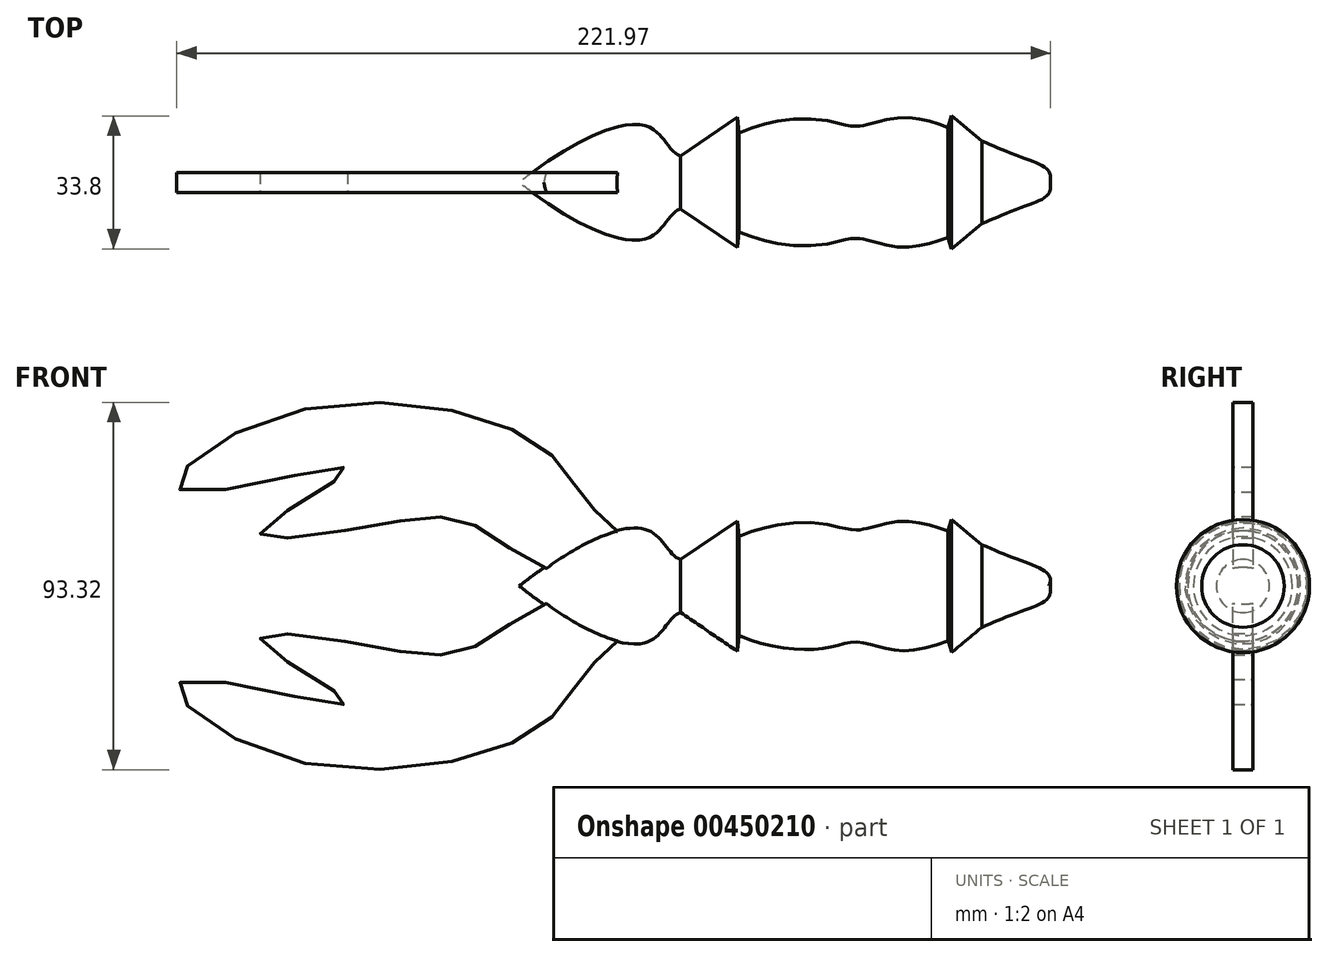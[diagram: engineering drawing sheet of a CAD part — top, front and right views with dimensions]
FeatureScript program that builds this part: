
annotation { "Feature Type Name" : "Feature", "Feature Type Description" : "" }
export const myFeature = defineFeature(function(context is Context, id is Id, definition is map)
    precondition{}
    {
        {
            var Q0;
            Q0=qCreatedBy(makeId("Front.planeOp"),FACE);
            var sketch = newSketch(context, id + "F0", { "sketchPlane" : qUnion([Q0])});
            skFitSpline(sketch, "E0", {"points": [v(-77.57, 0) * mm, v(-44.09, 13.8) * mm, v(-36.58, 6.72) * mm, v(-20.7, 13) * mm, v(0, 15.78) * mm, v(8.64, 14.26) * mm, v(21, 16.45) * mm, v(48.3, 7.05) * mm, v(57.04, 0) * mm], "startDerivative": vector(233.97, 184.67) * mm, "endDerivative": vector(-52.98, -112.96) * mm});
            skLineSegment(sketch, "E1", {"start": v(57.04, 0) * mm, "end": v(-77.57, 0) * mm});
            skPoint(sketch, "E2", {"position": v(35.31, 12.45) * mm});
            skPoint(sketch, "E3", {"position": v(-15.2, 14.82) * mm});
            skPoint(sketch, "E4", {"position": v(-25.37, 10.74) * mm});
            skLineSegment(sketch, "E5.0", {"start": v(-36.58, 6.72) * mm, "end": v(-22.12, 16.58) * mm});
            skLineSegment(sketch, "E5.1", {"start": v(-22.12, 16.58) * mm, "end": v(-21.7, 12.56) * mm});
            skPoint(sketch, "E5.0.midPoint", {"position": v(-29.35, 11.65) * mm});
            skLineSegment(sketch, "E6.2", {"start": v(31.4, 13.93) * mm, "end": v(32.3, 16.9) * mm});
            skLineSegment(sketch, "E6.3", {"start": v(32.3, 16.9) * mm, "end": v(39.95, 10.5) * mm});
            skPoint(sketch, "E6.0.midPoint", {"position": v(33.2, 8.05) * mm});
            skSolve(sketch);
        }
        {
            var Q0;
            Q0=makeQuery(id+"F0.imprint","IMPRINT",FACE,{"disambiguationData":[TD([[makeQuery(id+"F0.imprint","IMPRINT",EDGE,{"derivedFrom":sQuery(id+"F0.wireOp",EDGE,"E0")}),-1.0]])]});
            var Q1;
            {var subQ0=sQuery(id+"F0.wireOp",EDGE,"E6.3");Q1=makeQuery(id+"F0.imprint","IMPRINT",FACE,{"disambiguationData":[TD([[makeQuery(id+"F0.imprint","IMPRINT",EDGE,{"derivedFrom":subQ0}),-1.0]])]});}
            var Q2;
            {var subQ0=sQuery(id+"F0.wireOp",EDGE,"E5.0");Q2=makeQuery(id+"F0.imprint","IMPRINT",FACE,{"disambiguationData":[TD([[makeQuery(id+"F0.imprint","IMPRINT",EDGE,{"derivedFrom":subQ0}),-1.0]])]});}
            var Q3;
            Q3=sQuery(id+"F0.wireOp",EDGE,"E1");
            revolve(context, id + "F1", {"entities" : qUnion([Q0, Q1, Q2]), "axis" : qUnion([Q3]), "revolveType" : RevolveType.FULL});
        }
        {
            var Q0;
            Q0=qCreatedBy(makeId("Front.planeOp"),FACE);
            var sketch = newSketch(context, id + "F2", { "sketchPlane" : qUnion([Q0])});
            skFitSpline(sketch, "E7", {"points": [v(-51.57, 11.05) * mm, v(-59.58, 20.58) * mm, v(-72.55, 36) * mm, v(-140.06, 42.88) * mm, v(-163.1, 24.19) * mm, v(-121.13, 29.76) * mm, v(-143.2, 13.84) * mm, v(-114.56, 15.38) * mm, v(-89.23, 15.53) * mm, v(-66, 3.5) * mm, v(-51.57, 11.05) * mm]});
            skPoint(sketch, "E8", {"position": v(-105.78, 46.25) * mm});
            skSolve(sketch);
        }
        {
            var Q0;
            Q0=makeQuery(id+"F2.imprint","IMPRINT",FACE,{"disambiguationData":[TD([[makeQuery(id+"F2.imprint","IMPRINT",EDGE,{"derivedFrom":sQuery(id+"F2.wireOp",EDGE,"E7")}),1.0]])]});
            extrude(context, id + "F3", {"entities" : qUnion([Q0]), "operationType" : NewBodyOperationType.ADD, "depth" : 5.08 * mm, "symmetric" : true});
        }
        {
            var Q0;
            Q0=makeQuery(id+"F1.opRevolve","SWEPT_BODY",BODY,{"disambiguationData":[OSD([sQuery(id+"F0.wireOp",EDGE,"E0"),sQuery(id+"F0.wireOp",EDGE,"E1")])]});
            var Q1;
            Q1=qCreatedBy(makeId("Top.planeOp"),FACE);
            mirror(context, id + "F4", {"operationType" : NewBodyOperationType.ADD, "entities" : qUnion([Q0]), "mirrorPlane" : qUnion([Q1])});
        }
    });
